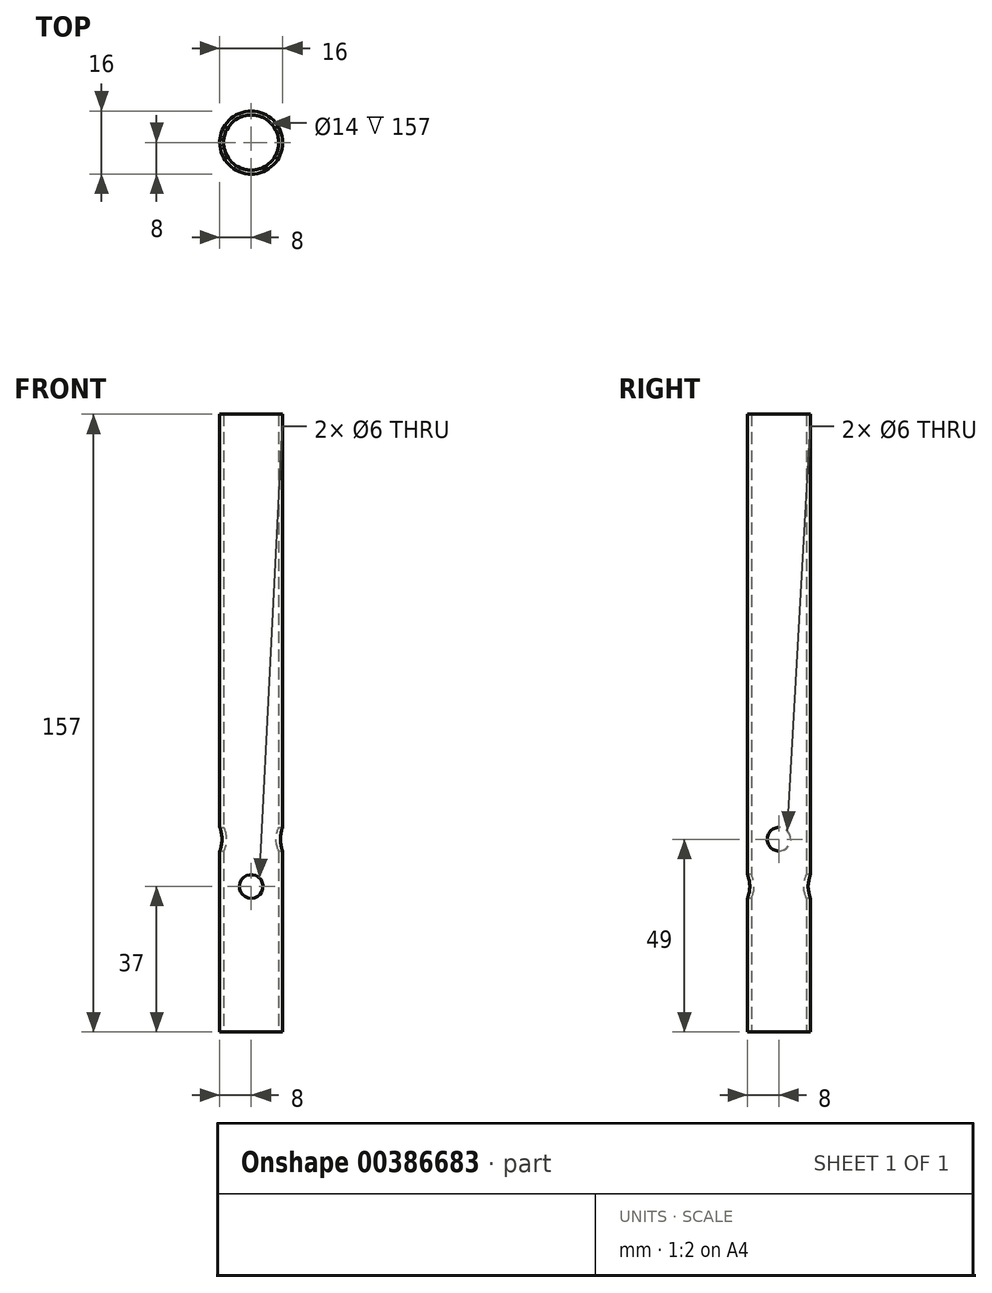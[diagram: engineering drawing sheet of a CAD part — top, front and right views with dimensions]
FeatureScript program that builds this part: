
annotation { "Feature Type Name" : "Feature", "Feature Type Description" : "" }
export const myFeature = defineFeature(function(context is Context, id is Id, definition is map)
    precondition{}
    {
        {
            var Q0;
            Q0=qCreatedBy(makeId("Top.planeOp"),FACE);
            var sketch = newSketch(context, id + "F0", { "sketchPlane" : qUnion([Q0])});
            skCircle(sketch, "E0", {"center": v(0, 0) * mm, "radius": 8 * mm});
            skCircle(sketch, "E1", {"center": v(0, 0) * mm, "radius": 7 * mm});
            skSolve(sketch);
        }
        {
            var Q0;
            Q0 = qSketchRegion(id + "F0", true);
            extrude(context, id + "F1", {"entities" : qUnion([Q0]), "depth" : 157 * mm});
        }
        {
            var Q0;
            Q0=qCreatedBy(makeId("Front.planeOp"),FACE);
            var sketch = newSketch(context, id + "F2", { "sketchPlane" : qUnion([Q0])});
            skCircle(sketch, "E2", {"center": v(0, 37) * mm, "radius": 3 * mm});
            skSolve(sketch);
        }
        {
            var Q0;
            Q0 = qSketchRegion(id + "F2", true);
            extrude(context, id + "F3", {"entities" : qUnion([Q0]), "operationType" : NewBodyOperationType.REMOVE, "endBound" : BoundingType.SYMMETRIC, "oppositeDirection" : true, "depth" : 50 * mm});
        }
        {
            var Q0;
            Q0=qCreatedBy(makeId("Right.planeOp"),FACE);
            var sketch = newSketch(context, id + "F4", { "sketchPlane" : qUnion([Q0])});
            skCircle(sketch, "E3", {"center": v(0, 49) * mm, "radius": 3 * mm});
            skSolve(sketch);
        }
        {
            var Q0;
            Q0 = qSketchRegion(id + "F4", true);
            extrude(context, id + "F5", {"entities" : qUnion([Q0]), "operationType" : NewBodyOperationType.REMOVE, "endBound" : BoundingType.SYMMETRIC, "oppositeDirection" : true, "depth" : 25 * mm});
        }
    });
